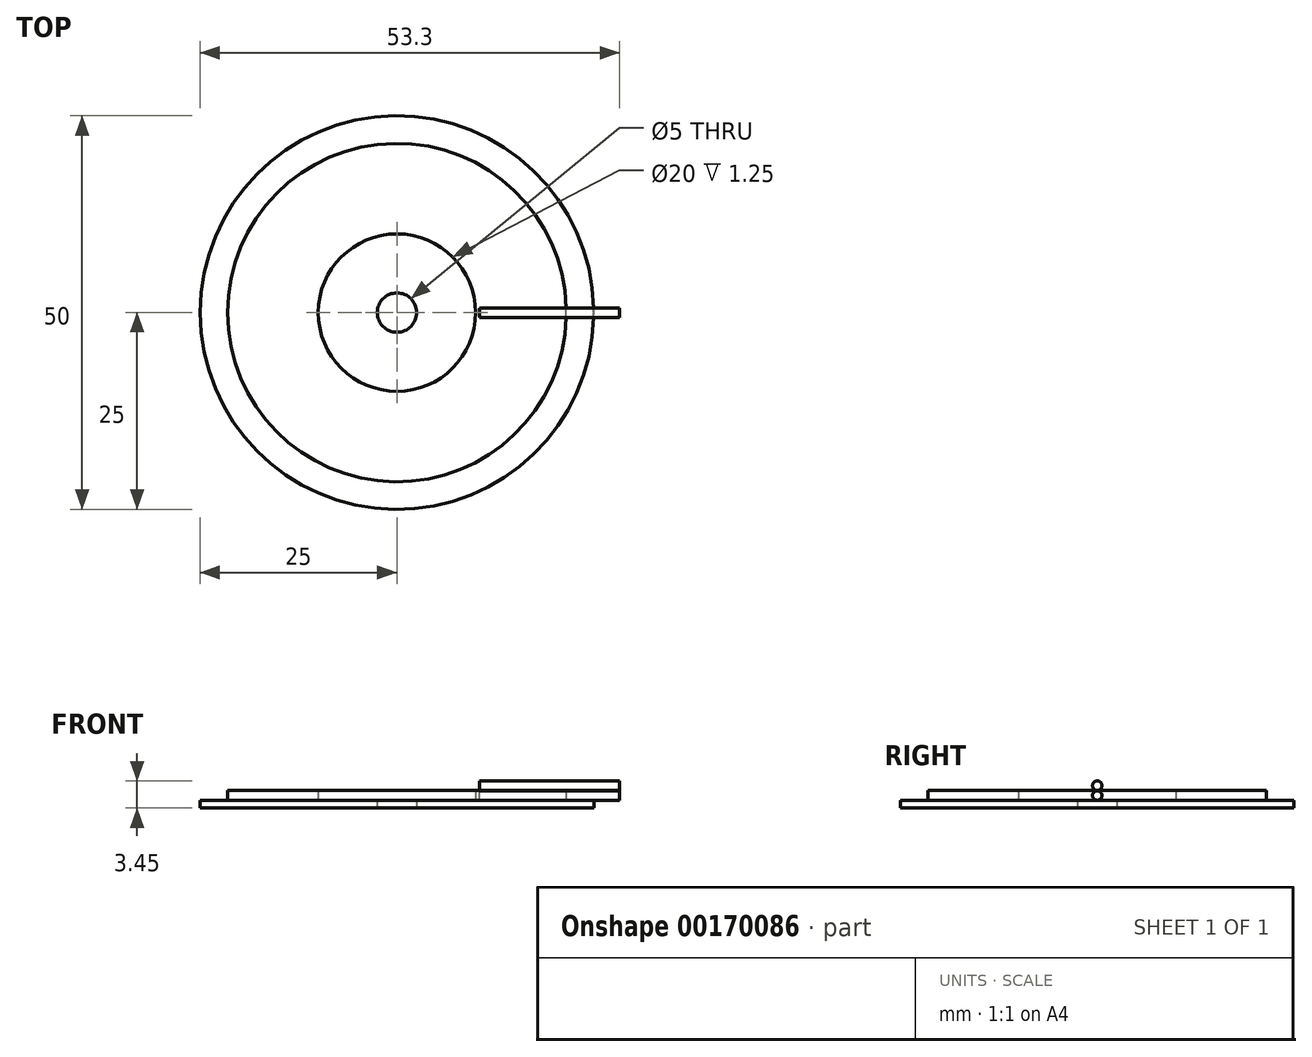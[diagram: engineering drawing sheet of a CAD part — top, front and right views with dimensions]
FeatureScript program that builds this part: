
annotation { "Feature Type Name" : "Feature", "Feature Type Description" : "" }
export const myFeature = defineFeature(function(context is Context, id is Id, definition is map)
    precondition{}
    {
        {
            var Q0;
            Q0=qCreatedBy(makeId("Top.planeOp"),FACE);
            var sketch = newSketch(context, id + "F0", { "sketchPlane" : qUnion([Q0])});
            skCircle(sketch, "E0", {"center": v(0, 0) * mm, "radius": 2.5 * mm});
            skCircle(sketch, "E1", {"center": v(0, 0) * mm, "radius": 25 * mm});
            skSolve(sketch);
        }
        {
            var Q0;
            Q0 = qSketchRegion(id + "F0", true);
            extrude(context, id + "F1", {"entities" : qUnion([Q0]), "depth" : 1 * mm});
        }
        {
            var Q0;
            Q0=makeQuery(id+"F1.opExtrude","CAP_FACE",FACE,{"disambiguationData":[OSD([sQuery(id+"F0.wireOp",EDGE,"E0"),sQuery(id+"F0.wireOp",EDGE,"E1")])],"isStart":false});
            var sketch = newSketch(context, id + "F2", { "sketchPlane" : qUnion([Q0])});
            skCircle(sketch, "E2", {"center": v(0, 0) * mm, "radius": 10 * mm});
            skCircle(sketch, "E3", {"center": v(0, 0) * mm, "radius": 21.5 * mm});
            skSolve(sketch);
        }
        {
            var Q0;
            Q0 = qSketchRegion(id + "F2", true);
            extrude(context, id + "F3", {"entities" : qUnion([Q0]), "operationType" : NewBodyOperationType.ADD, "depth" : 1.25 * mm});
        }
        {
            var Q0;
            Q0=qCreatedBy(makeId("Right.planeOp"),FACE);
            var sketch = newSketch(context, id + "F4", { "sketchPlane" : qUnion([Q0])});
            skCircle(sketch, "E4", {"center": v(0, 1.6) * mm, "radius": 0.6 * mm});
            skCircle(sketch, "E5", {"center": v(0, 2.85) * mm, "radius": 0.6 * mm});
            skSolve(sketch);
        }
        {
            var Q0;
            Q0 = qSketchRegion(id + "F4", true);
            extrude(context, id + "F5", {"entities" : qUnion([Q0]), "depth" : 28.3 * mm, "hasSecondDirection" : true, "secondDirectionOppositeDirection" : false, "secondDirectionDepth" : 10.5 * mm});
        }
    });
